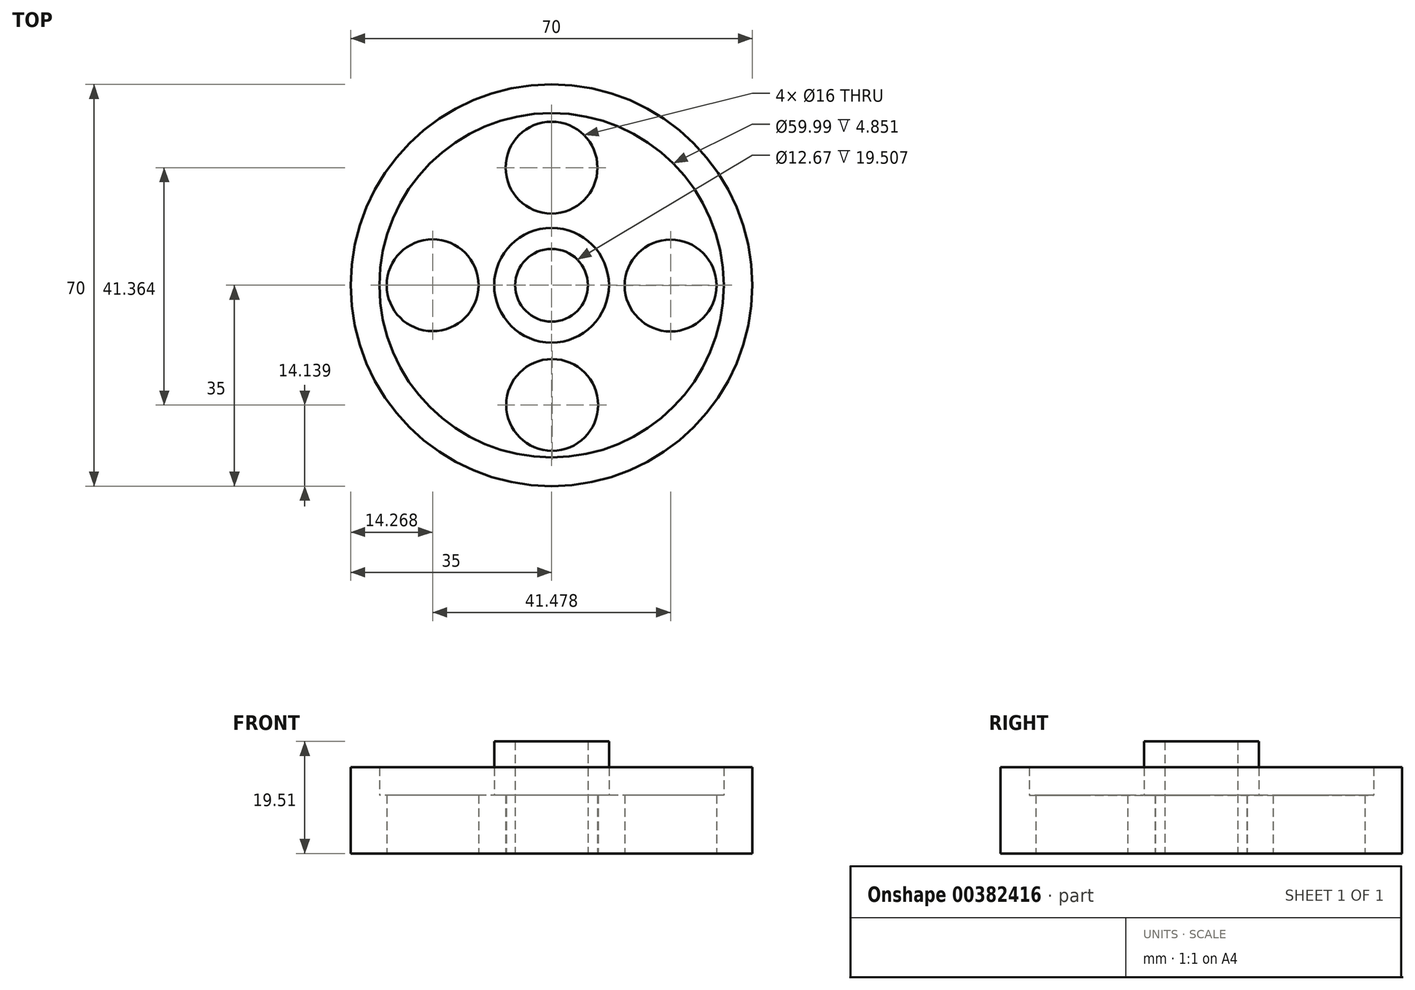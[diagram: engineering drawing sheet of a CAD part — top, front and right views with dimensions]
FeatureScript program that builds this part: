
annotation { "Feature Type Name" : "Feature", "Feature Type Description" : "" }
export const myFeature = defineFeature(function(context is Context, id is Id, definition is map)
    precondition{}
    {
        {
            var Q0;
            Q0=qCreatedBy(makeId("Top.planeOp"),FACE);
            var sketch = newSketch(context, id + "F0", { "sketchPlane" : qUnion([Q0])});
            skCircle(sketch, "E0", {"center": v(0, 0) * mm, "radius": 35 * mm});
            skCircle(sketch, "E1", {"center": v(0, 0) * mm, "radius": 30 * mm});
            skCircle(sketch, "E2", {"center": v(0, 0) * mm, "radius": 10 * mm});
            skCircle(sketch, "E3", {"center": v(0, 0) * mm, "radius": 6.34 * mm});
            skPoint(sketch, "E4.0.midPoint", {"position": v(0, 20.5) * mm});
            skCircle(sketch, "E5", {"center": v(-20.73, 0) * mm, "radius": 8 * mm});
            skCircle(sketch, "E6", {"center": v(0, 20.5) * mm, "radius": 8 * mm});
            skCircle(sketch, "E7", {"center": v(20.75, -0.05) * mm, "radius": 8 * mm});
            skCircle(sketch, "E8", {"center": v(0.1, -20.86) * mm, "radius": 8 * mm});
            skSolve(sketch);
        }
        {
            var Q0;
            {var subQ0=sQuery(id+"F0.wireOp",EDGE,"E4.0");var subQ1=sQuery(id+"F0.wireOp",EDGE,"E1");var subQ2=makeQuery(id+"F0.imprint","INTERSECT",VERTEX,{"disambiguationData":[OD(1.0)],"derivedFrom":[subQ1,subQ0]});Q0=makeQuery(id+"F0.imprint","IMPRINT",FACE,{"disambiguationData":[TD([[makeQuery(id+"F0.imprint","IMPRINT",EDGE,{"disambiguationData":[TD([[subQ2,-1.0]])],"derivedFrom":subQ1}),-1.0]])]});}
            var Q1;
            {var subQ0=sQuery(id+"F0.wireOp",EDGE,"E4.1");var subQ1=sQuery(id+"F0.wireOp",EDGE,"E1");var subQ2=makeQuery(id+"F0.imprint","INTERSECT",VERTEX,{"disambiguationData":[OD(0.0)],"derivedFrom":[subQ1,subQ0]});Q1=makeQuery(id+"F0.imprint","IMPRINT",FACE,{"disambiguationData":[TD([[makeQuery(id+"F0.imprint","IMPRINT",EDGE,{"disambiguationData":[TD([[subQ2,-1.0]])],"derivedFrom":subQ1}),-1.0]])]});}
            var Q2;
            {var subQ0=sQuery(id+"F0.wireOp",EDGE,"E4.2");var subQ1=sQuery(id+"F0.wireOp",EDGE,"E1");var subQ2=makeQuery(id+"F0.imprint","INTERSECT",VERTEX,{"disambiguationData":[OD(1.0)],"derivedFrom":[subQ1,subQ0]});Q2=makeQuery(id+"F0.imprint","IMPRINT",FACE,{"disambiguationData":[TD([[makeQuery(id+"F0.imprint","IMPRINT",EDGE,{"disambiguationData":[TD([[subQ2,-1.0]])],"derivedFrom":subQ1}),-1.0]])]});}
            var Q3;
            Q3=makeQuery(id+"F0.imprint","IMPRINT",FACE,{"disambiguationData":[TD([[makeQuery(id+"F0.imprint","IMPRINT",EDGE,{"derivedFrom":sQuery(id+"F0.wireOp",EDGE,"E0")}),1.0]])]});
            var Q4;
            {var subQ0=sQuery(id+"F0.wireOp",EDGE,"E4.3");var subQ1=sQuery(id+"F0.wireOp",EDGE,"E1");var subQ2=makeQuery(id+"F0.imprint","INTERSECT",VERTEX,{"disambiguationData":[OD(1.0)],"derivedFrom":[subQ1,subQ0]});Q4=makeQuery(id+"F0.imprint","IMPRINT",FACE,{"disambiguationData":[TD([[makeQuery(id+"F0.imprint","IMPRINT",EDGE,{"disambiguationData":[TD([[subQ2,-1.0]])],"derivedFrom":subQ1}),-1.0]])]});}
            extrude(context, id + "F1", {"entities" : qUnion([Q0, Q1, Q2, Q3, Q4]), "depth" : 15 * mm});
        }
        {
            var Q0;
            Q0=makeQuery(id+"F0.imprint","IMPRINT",FACE,{"disambiguationData":[TD([[makeQuery(id+"F0.imprint","IMPRINT",EDGE,{"derivedFrom":sQuery(id+"F0.wireOp",EDGE,"E1")}),1.0]])]});
            extrude(context, id + "F2", {"entities" : qUnion([Q0]), "operationType" : NewBodyOperationType.ADD, "depth" : 10.16 * mm});
        }
        {
            var Q0;
            Q0=makeQuery(id+"F0.imprint","IMPRINT",FACE,{"disambiguationData":[TD([[makeQuery(id+"F0.imprint","IMPRINT",EDGE,{"derivedFrom":sQuery(id+"F0.wireOp",EDGE,"E2")}),1.0]])]});
            extrude(context, id + "F3", {"entities" : qUnion([Q0]), "operationType" : NewBodyOperationType.ADD, "depth" : 19.5 * mm});
        }
    });
